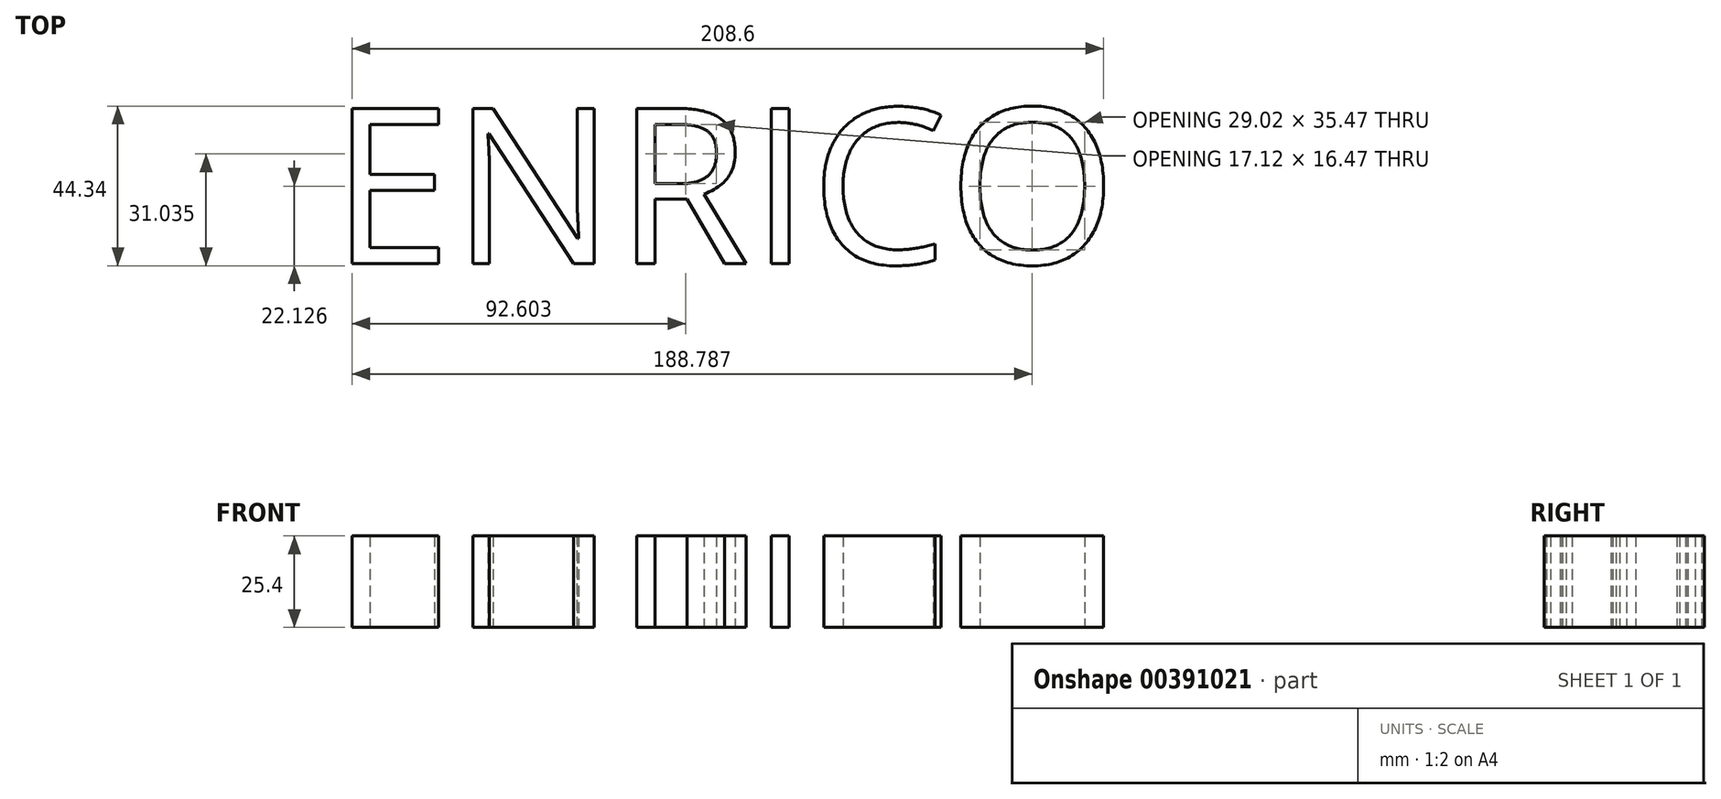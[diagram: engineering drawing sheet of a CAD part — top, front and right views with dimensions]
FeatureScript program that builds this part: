
annotation { "Feature Type Name" : "Feature", "Feature Type Description" : "" }
export const myFeature = defineFeature(function(context is Context, id is Id, definition is map)
    precondition{}
    {
        {
            var Q0;
            Q0=qCreatedBy(makeId("Top.planeOp"),FACE);
            var sketch = newSketch(context, id + "F0", { "sketchPlane" : qUnion([Q0])});
            skText(sketch, "E0", { "text": "ENRICO", "fontName": "OpenSans-Regular.ttf"});
            const initialGuessF0  = {"E0": [-0.0172, -0.04344, 1, 0, 0.04344]};
            skSetInitialGuess(sketch, initialGuessF0);
            skSolve(sketch);
        }
        {
            var Q0;
            Q0 = qSketchRegion(id + "F0", true);
            extrude(context, id + "F1", {"entities" : qUnion([Q0]), "depth" : 25.4 * mm});
        }
    });
